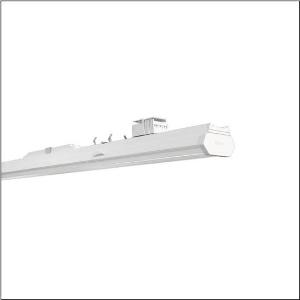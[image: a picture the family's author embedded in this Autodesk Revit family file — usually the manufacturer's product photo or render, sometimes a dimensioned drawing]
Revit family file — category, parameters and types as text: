
# Revit family: licross_r__11_protected_ho_51tp12mn4f5m_a747
name_source: partatom
category: Lighting Fixtures
units: mm (PartAtom-declared; Revit-internal decimal feet)

## family parameters
Cut with Voids When Loaded = No
Host = Face
Light Source = No
Part Type = Normal
Room Calculation Point = No
Round Connector Dimension = Use Diameter
Shared = No

## types (1)
- --- (1 x LED, 15820 lm, 87.4 W, 4000K)
    Apparent Load = 87 VA
    CIE Flux Codes = 70 91 97 98 100
    Color Rendering = 80
    Color Temperature = 4000K
    Default Elevation = 1800 mm
    Description = Licross® 11 Protected HO, luminaire insert, of sheet steel, galvanised, coil coated, white, length: 1.500mm, width: 90mm, height: 101mm, LED rated luminous flux: 15.820lm, light colour: 840, control gear: ON/OFF Multilumen, with plug, 3-pole, with phase selection, mains connection: 220..240V, AC, 50/60Hz, rated input power: 87W, halogen-free wiring, primary light control with lens, of plastic, primary optical cover: cover, of PMMA, light emission: direct distribution, primary light characteristic: symmetric, protection rating (complete): IP64, insulation class (complete): insulation class I (protective earthing), certification: CE, ENEC, VDE, UKCA, protection symbol: D if used in an environment with conductive dust loads with corresponding accessories, impact resistance: IK06, permissible ambient temperature for indoor applications: -35..+35°C, corresponds to IFS (International Featured Standards) requirements for safety and quality in the food industry, reducing of maximum allowable ambient temperature of 5°C with ceiling mounting, LABS conformity tested according to VDMA 24364:2018-05, packaging unit: 1 piece
    Height = 92 mm
    Lamp = 1 x LED
    Lamp Light Flux = 15820 lm
    Lamp Power = 87.4 W
    Lamp count = 1
    Length = 1500 mm
    Luminous efficacy = 181 lm/W
    Manufacturer = Siteco
    ModVariant = No
    Model = 51TP12MN4F5M
    Mounting Place = Ceiling
    Mounting Type = Pendant
    Number of Poles = 1
    OnlyDefault = Yes
    Power Factor = 1
    Product Name = Licross® 11 Protected HO
    Product group = luminaire insert
    ProductGroupID = 901
    Protection Class = Protection class I
    Protection Degree = IP 64
    RLX_Detail_Level = 1
    RLX_Emergency_Light_Flux = 0 lm
    RLX_Emergency_Type = 0
    RLX_Emergency_Type_DB = No
    RlxData = <blob elided: 22073 chars, md5=39a55e04>
    Socket = socket
    Standby Power = 0 W
    System Light Flux = 15820 lm
    System Power = 87 W
    Type Comments = factory setting: luminous flux: 100 % | (A | C | E) | 203 mA
    Type Image = l_1256148.jpg
    URL = http://relux.com
    VarID = @adj_055335
    Voltage = 0 V
    Weight = 0.00 kg
    Width = 88 mm

## geometry (parser evidence)
native form markers: Blend x4, Sweep x10
no freeform markers — native parametric forms only
